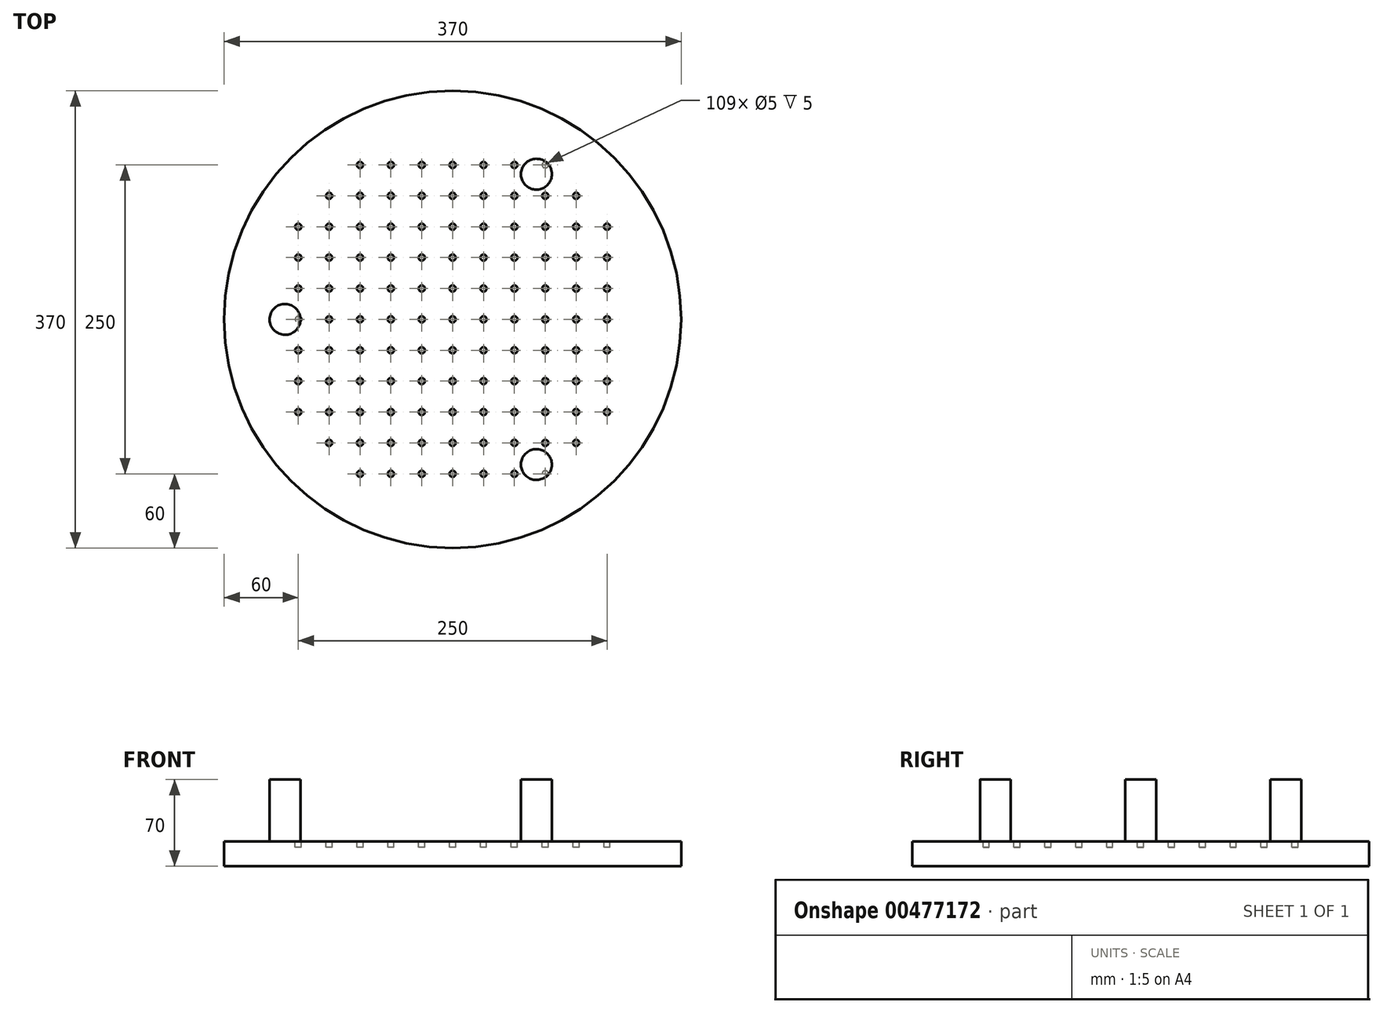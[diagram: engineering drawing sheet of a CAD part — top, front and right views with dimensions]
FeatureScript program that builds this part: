
annotation { "Feature Type Name" : "Feature", "Feature Type Description" : "" }
export const myFeature = defineFeature(function(context is Context, id is Id, definition is map)
    precondition{}
    {
        {
            var Q0;
            Q0=qCreatedBy(makeId("Top.planeOp"),FACE);
            var sketch = newSketch(context, id + "F0", { "sketchPlane" : qUnion([Q0])});
            skCircle(sketch, "E0", {"center": v(0, 0) * mm, "radius": 185 * mm});
            skSolve(sketch);
        }
        {
            var Q0;
            Q0=makeQuery(id+"F0.imprint","IMPRINT",FACE,{"disambiguationData":[TD([[makeQuery(id+"F0.imprint","IMPRINT",EDGE,{"derivedFrom":sQuery(id+"F0.wireOp",EDGE,"E0")}),1.0]])]});
            extrude(context, id + "F1", {"entities" : qUnion([Q0]), "depth" : 20 * mm});
        }
        {
            var Q0;
            Q0=makeQuery(id+"F1.opExtrude","CAP_FACE",FACE,{"disambiguationData":[OSD([sQuery(id+"F0.wireOp",EDGE,"E0")])],"isStart":false});
            var sketch = newSketch(context, id + "F2", { "sketchPlane" : qUnion([Q0])});
            skCircle(sketch, "E1", {"center": v(0, 0) * mm, "radius": 160 * mm});
            skCircle(sketch, "E2.0", {"center": v(0, 0) * mm, "radius": 157 * mm});
            skSolve(sketch);
        }
        {
            var Q0;
            Q0=sQuery(id+"F2.wireOp",EDGE,"E1");
            var Q1;
            Q1=sQuery(id+"F2.wireOp",EDGE,"E2.0");
            extrude(context, id + "F3", {"bodyType" : ToolBodyType.SURFACE, "surfaceEntities" : qUnion([Q0, Q1]), "oppositeDirection" : true, "depth" : 5 * mm});
        }
        {
            var Q0;
            Q0=makeQuery(id+"F1.opExtrude","CAP_FACE",FACE,{"disambiguationData":[OSD([sQuery(id+"F0.wireOp",EDGE,"E0")])],"isStart":false});
            var sketch = newSketch(context, id + "F4", { "sketchPlane" : qUnion([Q0])});
            skCircle(sketch, "E3", {"center": v(0, 0) * mm, "radius": 2.5 * mm});
            skCircle(sketch, "E4.0.1.0", {"center": v(0, 25) * mm, "radius": 2.5 * mm});
            skCircle(sketch, "E4.0.2.0", {"center": v(0, 50) * mm, "radius": 2.5 * mm});
            skCircle(sketch, "E4.0.3.0", {"center": v(0, 75) * mm, "radius": 2.5 * mm});
            skCircle(sketch, "E4.0.4.0", {"center": v(0, 100) * mm, "radius": 2.5 * mm});
            skCircle(sketch, "E4.0.5.0", {"center": v(0, 125) * mm, "radius": 2.5 * mm});
            skCircle(sketch, "E4.1.0.0", {"center": v(25, 0) * mm, "radius": 2.5 * mm});
            skCircle(sketch, "E4.1.1.0", {"center": v(25, 25) * mm, "radius": 2.5 * mm});
            skCircle(sketch, "E4.1.2.0", {"center": v(25, 50) * mm, "radius": 2.5 * mm});
            skCircle(sketch, "E4.1.3.0", {"center": v(25, 75) * mm, "radius": 2.5 * mm});
            skCircle(sketch, "E4.1.4.0", {"center": v(25, 100) * mm, "radius": 2.5 * mm});
            skCircle(sketch, "E4.1.5.0", {"center": v(25, 125) * mm, "radius": 2.5 * mm});
            skCircle(sketch, "E4.2.0.0", {"center": v(50, 0) * mm, "radius": 2.5 * mm});
            skCircle(sketch, "E4.2.1.0", {"center": v(50, 25) * mm, "radius": 2.5 * mm});
            skCircle(sketch, "E4.2.2.0", {"center": v(50, 50) * mm, "radius": 2.5 * mm});
            skCircle(sketch, "E4.2.3.0", {"center": v(50, 75) * mm, "radius": 2.5 * mm});
            skCircle(sketch, "E4.2.4.0", {"center": v(50, 100) * mm, "radius": 2.5 * mm});
            skCircle(sketch, "E4.2.5.0", {"center": v(50, 125) * mm, "radius": 2.5 * mm});
            skCircle(sketch, "E4.3.0.0", {"center": v(75, 0) * mm, "radius": 2.5 * mm});
            skCircle(sketch, "E4.3.1.0", {"center": v(75, 25) * mm, "radius": 2.5 * mm});
            skCircle(sketch, "E4.3.2.0", {"center": v(75, 50) * mm, "radius": 2.5 * mm});
            skCircle(sketch, "E4.3.3.0", {"center": v(75, 75) * mm, "radius": 2.5 * mm});
            skCircle(sketch, "E4.3.4.0", {"center": v(75, 100) * mm, "radius": 2.5 * mm});
            skCircle(sketch, "E4.3.5.0", {"center": v(75, 125) * mm, "radius": 2.5 * mm});
            skCircle(sketch, "E4.4.0.0", {"center": v(100, 0) * mm, "radius": 2.5 * mm});
            skCircle(sketch, "E4.4.1.0", {"center": v(100, 25) * mm, "radius": 2.5 * mm});
            skCircle(sketch, "E4.4.2.0", {"center": v(100, 50) * mm, "radius": 2.5 * mm});
            skCircle(sketch, "E4.4.3.0", {"center": v(100, 75) * mm, "radius": 2.5 * mm});
            skCircle(sketch, "E4.4.4.0", {"center": v(100, 100) * mm, "radius": 2.5 * mm});
            skCircle(sketch, "E4.5.0.0", {"center": v(125, 0) * mm, "radius": 2.5 * mm});
            skCircle(sketch, "E4.5.1.0", {"center": v(125, 25) * mm, "radius": 2.5 * mm});
            skCircle(sketch, "E4.5.2.0", {"center": v(125, 50) * mm, "radius": 2.5 * mm});
            skCircle(sketch, "E4.5.3.0", {"center": v(125, 75) * mm, "radius": 2.5 * mm});
            skLineSegment(sketch, "E4.direction1", {"start": v(0, 0) * mm, "end": v(25, 0) * mm, "construction": true});
            skLineSegment(sketch, "E4.direction2", {"start": v(0, 0) * mm, "end": v(0, 25) * mm, "construction": true});
            skLineSegment(sketch, "E5.1.0", {"start": v(0, 0) * mm, "end": v(0, -25) * mm, "construction": true});
            skCircle(sketch, "E5.1.2", {"center": v(75, -25) * mm, "radius": 2.5 * mm});
            skCircle(sketch, "E5.1.3", {"center": v(100, -50) * mm, "radius": 2.5 * mm});
            skCircle(sketch, "E5.1.4", {"center": v(0, -100) * mm, "radius": 2.5 * mm});
            skCircle(sketch, "E5.1.5", {"center": v(100, -100) * mm, "radius": 2.5 * mm});
            skCircle(sketch, "E5.1.6", {"center": v(75, -100) * mm, "radius": 2.5 * mm});
            skCircle(sketch, "E5.1.7", {"center": v(125, -50) * mm, "radius": 2.5 * mm});
            skCircle(sketch, "E5.1.8", {"center": v(75, -125) * mm, "radius": 2.5 * mm});
            skCircle(sketch, "E5.1.10", {"center": v(25, -50) * mm, "radius": 2.5 * mm});
            skCircle(sketch, "E5.1.12", {"center": v(0, -75) * mm, "radius": 2.5 * mm});
            skCircle(sketch, "E5.1.14", {"center": v(100, -75) * mm, "radius": 2.5 * mm});
            skCircle(sketch, "E5.1.16", {"center": v(100, -25) * mm, "radius": 2.5 * mm});
            skCircle(sketch, "E5.1.17", {"center": v(50, -125) * mm, "radius": 2.5 * mm});
            skCircle(sketch, "E5.1.18", {"center": v(125, -25) * mm, "radius": 2.5 * mm});
            skCircle(sketch, "E5.1.19", {"center": v(50, -75) * mm, "radius": 2.5 * mm});
            skCircle(sketch, "E5.1.20", {"center": v(25, -25) * mm, "radius": 2.5 * mm});
            skCircle(sketch, "E5.1.21", {"center": v(75, -75) * mm, "radius": 2.5 * mm});
            skCircle(sketch, "E5.1.22", {"center": v(75, -50) * mm, "radius": 2.5 * mm});
            skCircle(sketch, "E5.1.23", {"center": v(125, -75) * mm, "radius": 2.5 * mm});
            skCircle(sketch, "E5.1.24", {"center": v(0, -125) * mm, "radius": 2.5 * mm});
            skCircle(sketch, "E5.1.25", {"center": v(25, -75) * mm, "radius": 2.5 * mm});
            skCircle(sketch, "E5.1.26", {"center": v(50, -100) * mm, "radius": 2.5 * mm});
            skCircle(sketch, "E5.1.27", {"center": v(25, -125) * mm, "radius": 2.5 * mm});
            skCircle(sketch, "E5.1.28", {"center": v(0, -50) * mm, "radius": 2.5 * mm});
            skCircle(sketch, "E5.1.29", {"center": v(25, -100) * mm, "radius": 2.5 * mm});
            skCircle(sketch, "E5.1.30", {"center": v(50, -25) * mm, "radius": 2.5 * mm});
            skCircle(sketch, "E5.1.31", {"center": v(50, -50) * mm, "radius": 2.5 * mm});
            skCircle(sketch, "E5.1.32", {"center": v(0, -25) * mm, "radius": 2.5 * mm});
            skLineSegment(sketch, "E5.2.0", {"start": v(0, 0) * mm, "end": v(-25, 0) * mm, "construction": true});
            skLineSegment(sketch, "E5.2.1", {"start": v(0, 0) * mm, "end": v(0, -25) * mm, "construction": true});
            skCircle(sketch, "E5.2.2", {"center": v(-25, -75) * mm, "radius": 2.5 * mm});
            skCircle(sketch, "E5.2.3", {"center": v(-50, -100) * mm, "radius": 2.5 * mm});
            skCircle(sketch, "E5.2.4", {"center": v(-100, 0) * mm, "radius": 2.5 * mm});
            skCircle(sketch, "E5.2.5", {"center": v(-100, -100) * mm, "radius": 2.5 * mm});
            skCircle(sketch, "E5.2.6", {"center": v(-100, -75) * mm, "radius": 2.5 * mm});
            skCircle(sketch, "E5.2.7", {"center": v(-50, -125) * mm, "radius": 2.5 * mm});
            skCircle(sketch, "E5.2.8", {"center": v(-125, -75) * mm, "radius": 2.5 * mm});
            skCircle(sketch, "E5.2.9", {"center": v(0, -75) * mm, "radius": 2.5 * mm});
            skCircle(sketch, "E5.2.10", {"center": v(-50, -25) * mm, "radius": 2.5 * mm});
            skCircle(sketch, "E5.2.11", {"center": v(0, -100) * mm, "radius": 2.5 * mm});
            skCircle(sketch, "E5.2.12", {"center": v(-75, 0) * mm, "radius": 2.5 * mm});
            skCircle(sketch, "E5.2.13", {"center": v(0, -125) * mm, "radius": 2.5 * mm});
            skCircle(sketch, "E5.2.14", {"center": v(-75, -100) * mm, "radius": 2.5 * mm});
            skCircle(sketch, "E5.2.15", {"center": v(0, -50) * mm, "radius": 2.5 * mm});
            skCircle(sketch, "E5.2.16", {"center": v(-25, -100) * mm, "radius": 2.5 * mm});
            skCircle(sketch, "E5.2.17", {"center": v(-125, -50) * mm, "radius": 2.5 * mm});
            skCircle(sketch, "E5.2.18", {"center": v(-25, -125) * mm, "radius": 2.5 * mm});
            skCircle(sketch, "E5.2.19", {"center": v(-75, -50) * mm, "radius": 2.5 * mm});
            skCircle(sketch, "E5.2.20", {"center": v(-25, -25) * mm, "radius": 2.5 * mm});
            skCircle(sketch, "E5.2.21", {"center": v(-75, -75) * mm, "radius": 2.5 * mm});
            skCircle(sketch, "E5.2.22", {"center": v(-50, -75) * mm, "radius": 2.5 * mm});
            skCircle(sketch, "E5.2.23", {"center": v(-75, -125) * mm, "radius": 2.5 * mm});
            skCircle(sketch, "E5.2.24", {"center": v(-125, 0) * mm, "radius": 2.5 * mm});
            skCircle(sketch, "E5.2.25", {"center": v(-75, -25) * mm, "radius": 2.5 * mm});
            skCircle(sketch, "E5.2.26", {"center": v(-100, -50) * mm, "radius": 2.5 * mm});
            skCircle(sketch, "E5.2.27", {"center": v(-125, -25) * mm, "radius": 2.5 * mm});
            skCircle(sketch, "E5.2.28", {"center": v(-50, 0) * mm, "radius": 2.5 * mm});
            skCircle(sketch, "E5.2.29", {"center": v(-100, -25) * mm, "radius": 2.5 * mm});
            skCircle(sketch, "E5.2.30", {"center": v(-25, -50) * mm, "radius": 2.5 * mm});
            skCircle(sketch, "E5.2.31", {"center": v(-50, -50) * mm, "radius": 2.5 * mm});
            skCircle(sketch, "E5.2.32", {"center": v(-25, 0) * mm, "radius": 2.5 * mm});
            skCircle(sketch, "E5.2.33", {"center": v(0, -25) * mm, "radius": 2.5 * mm});
            skLineSegment(sketch, "E5.3.1", {"start": v(0, 0) * mm, "end": v(-25, 0) * mm, "construction": true});
            skCircle(sketch, "E5.3.2", {"center": v(-75, 25) * mm, "radius": 2.5 * mm});
            skCircle(sketch, "E5.3.3", {"center": v(-100, 50) * mm, "radius": 2.5 * mm});
            skCircle(sketch, "E5.3.5", {"center": v(-100, 100) * mm, "radius": 2.5 * mm});
            skCircle(sketch, "E5.3.6", {"center": v(-75, 100) * mm, "radius": 2.5 * mm});
            skCircle(sketch, "E5.3.7", {"center": v(-125, 50) * mm, "radius": 2.5 * mm});
            skCircle(sketch, "E5.3.8", {"center": v(-75, 125) * mm, "radius": 2.5 * mm});
            skCircle(sketch, "E5.3.9", {"center": v(-75, 0) * mm, "radius": 2.5 * mm});
            skCircle(sketch, "E5.3.10", {"center": v(-25, 50) * mm, "radius": 2.5 * mm});
            skCircle(sketch, "E5.3.11", {"center": v(-100, 0) * mm, "radius": 2.5 * mm});
            skCircle(sketch, "E5.3.13", {"center": v(-125, 0) * mm, "radius": 2.5 * mm});
            skCircle(sketch, "E5.3.14", {"center": v(-100, 75) * mm, "radius": 2.5 * mm});
            skCircle(sketch, "E5.3.15", {"center": v(-50, 0) * mm, "radius": 2.5 * mm});
            skCircle(sketch, "E5.3.16", {"center": v(-100, 25) * mm, "radius": 2.5 * mm});
            skCircle(sketch, "E5.3.17", {"center": v(-50, 125) * mm, "radius": 2.5 * mm});
            skCircle(sketch, "E5.3.18", {"center": v(-125, 25) * mm, "radius": 2.5 * mm});
            skCircle(sketch, "E5.3.19", {"center": v(-50, 75) * mm, "radius": 2.5 * mm});
            skCircle(sketch, "E5.3.20", {"center": v(-25, 25) * mm, "radius": 2.5 * mm});
            skCircle(sketch, "E5.3.21", {"center": v(-75, 75) * mm, "radius": 2.5 * mm});
            skCircle(sketch, "E5.3.22", {"center": v(-75, 50) * mm, "radius": 2.5 * mm});
            skCircle(sketch, "E5.3.23", {"center": v(-125, 75) * mm, "radius": 2.5 * mm});
            skCircle(sketch, "E5.3.25", {"center": v(-25, 75) * mm, "radius": 2.5 * mm});
            skCircle(sketch, "E5.3.26", {"center": v(-50, 100) * mm, "radius": 2.5 * mm});
            skCircle(sketch, "E5.3.27", {"center": v(-25, 125) * mm, "radius": 2.5 * mm});
            skCircle(sketch, "E5.3.29", {"center": v(-25, 100) * mm, "radius": 2.5 * mm});
            skCircle(sketch, "E5.3.30", {"center": v(-50, 25) * mm, "radius": 2.5 * mm});
            skCircle(sketch, "E5.3.31", {"center": v(-50, 50) * mm, "radius": 2.5 * mm});
            skCircle(sketch, "E5.3.33", {"center": v(-25, 0) * mm, "radius": 2.5 * mm});
            skSolve(sketch);
        }
        {
            var Q0;
            Q0=qSketchRegion(id+"F4",true);
            extrude(context, id + "F5", {"entities" : qUnion([Q0]), "operationType" : NewBodyOperationType.REMOVE, "oppositeDirection" : true, "depth" : 5 * mm});
        }
        {
            var Q0;
            Q0=makeQuery(id+"F1.opExtrude","CAP_FACE",FACE,{"disambiguationData":[OSD([sQuery(id+"F0.wireOp",EDGE,"E0")])],"isStart":false});
            var sketch = newSketch(context, id + "F6", { "sketchPlane" : qUnion([Q0])});
            skCircle(sketch, "E6", {"center": v(-135.68, 0) * mm, "radius": 12.5 * mm});
            skCircle(sketch, "E7.1.0", {"center": v(67.84, -117.5) * mm, "radius": 12.5 * mm});
            skCircle(sketch, "E7.2.0", {"center": v(67.84, 117.5) * mm, "radius": 12.5 * mm});
            skPoint(sketch, "E7.center", {"position": v(0, 0) * mm});
            skSolve(sketch);
        }
        {
            var Q0;
            Q0 = qSketchRegion(id + "F6", true);
            extrude(context, id + "F7", {"entities" : qUnion([Q0]), "operationType" : NewBodyOperationType.ADD, "depth" : 50 * mm});
        }
    });
